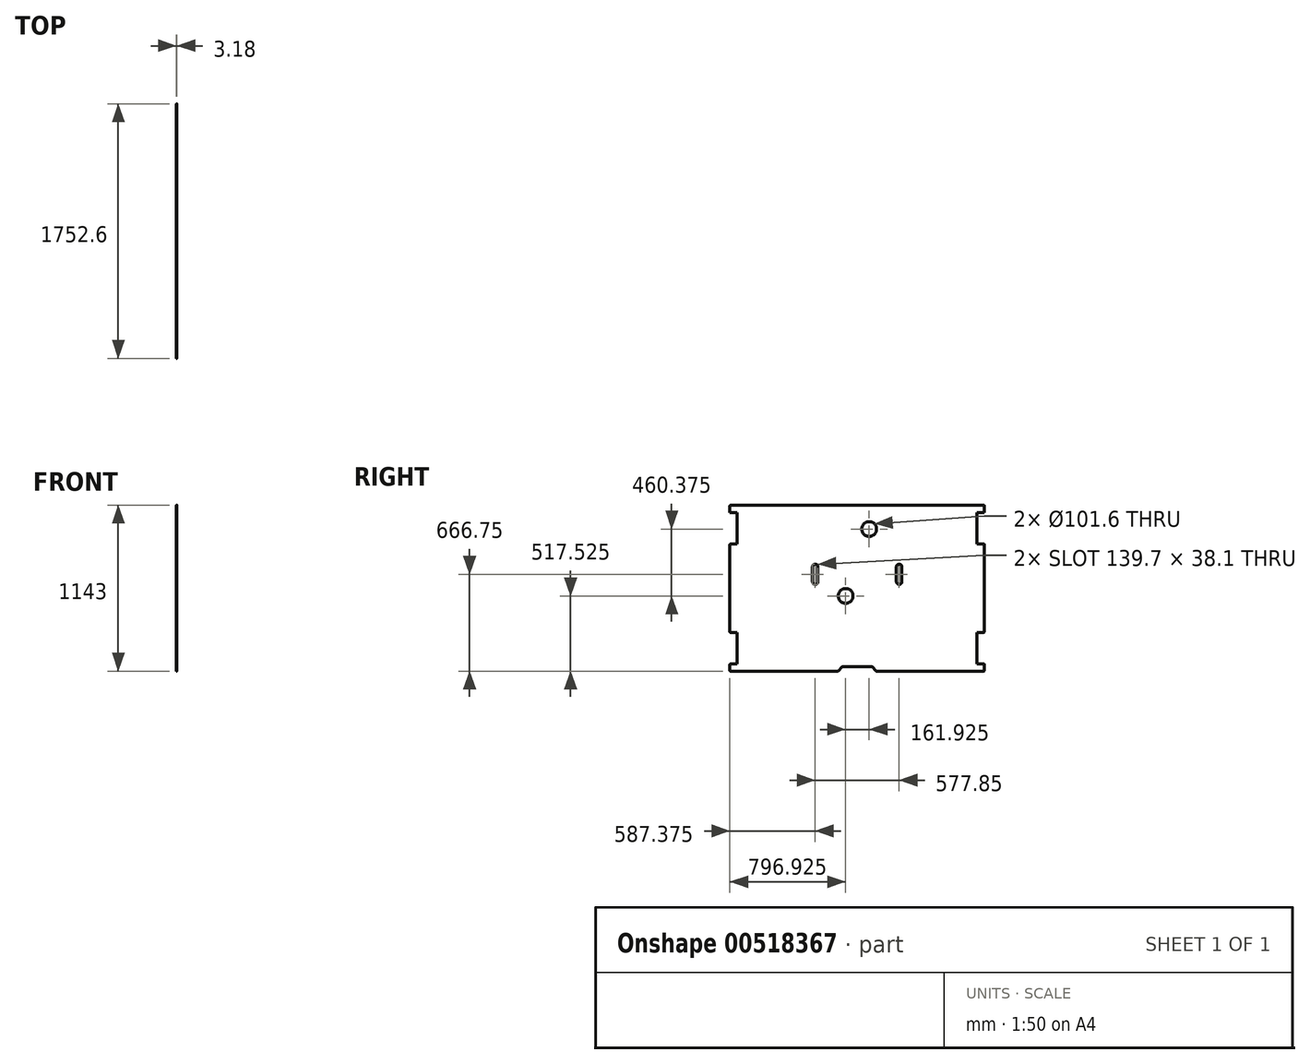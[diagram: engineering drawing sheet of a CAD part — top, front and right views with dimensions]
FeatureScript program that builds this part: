
annotation { "Feature Type Name" : "Feature", "Feature Type Description" : "" }
export const myFeature = defineFeature(function(context is Context, id is Id, definition is map)
    precondition{}
    {
        {
            var Q0;
            Q0=qCreatedBy(makeId("Right.planeOp"),FACE);
            var sketch = newSketch(context, id + "F0", { "sketchPlane" : qUnion([Q0])});
            skLineSegment(sketch, "E0.bottom", {"start": v(-876.3, 571.5) * mm, "end": v(876.3, 571.5) * mm});
            skLineSegment(sketch, "E0.top", {"start": v(-876.3, -571.5) * mm, "end": v(876.3, -571.5) * mm});
            skLineSegment(sketch, "E0.left", {"start": v(-876.3, 571.5) * mm, "end": v(-876.3, -571.5) * mm});
            skLineSegment(sketch, "E0.right", {"start": v(876.3, 571.5) * mm, "end": v(876.3, -571.5) * mm});
            skSolve(sketch);
        }
        {
            var Q0;
            Q0=makeQuery(id+"F0.imprint","IMPRINT",FACE,{"disambiguationData":[TD([[makeQuery(id+"F0.imprint","IMPRINT",EDGE,{"derivedFrom":sQuery(id+"F0.wireOp",EDGE,"E0.bottom")}),-1.0]])]});
            extrude(context, id + "F1", {"entities" : qUnion([Q0]), "endBound" : BoundingType.SYMMETRIC, "depth" : 3.17 * mm, "offsetDistance" : 25.4 * mm});
        }
        {
            var Q0;
            Q0=makeQuery(id+"F1.opExtrude","CAP_FACE",FACE,{"disambiguationData":[OSD([sQuery(id+"F0.wireOp",EDGE,"E0.bottom"),sQuery(id+"F0.wireOp",EDGE,"E0.top"),sQuery(id+"F0.wireOp",EDGE,"E0.left"),sQuery(id+"F0.wireOp",EDGE,"E0.right")])],"isStart":false});
            var sketch = newSketch(context, id + "F2", { "sketchPlane" : qUnion([Q0])});
            skLineSegment(sketch, "E1.bottom", {"start": v(-876.3, 520.7) * mm, "end": v(-825.5, 520.7) * mm});
            skLineSegment(sketch, "E1.top", {"start": v(-876.3, 304.8) * mm, "end": v(-825.5, 304.8) * mm});
            skLineSegment(sketch, "E1.left", {"start": v(-876.3, 520.7) * mm, "end": v(-876.3, 304.8) * mm});
            skLineSegment(sketch, "E1.right", {"start": v(-825.5, 520.7) * mm, "end": v(-825.5, 304.8) * mm});
            skLineSegment(sketch, "E2.MirrorCS", {"start": v(876.3, 304.8) * mm, "end": v(825.5, 304.8) * mm});
            skLineSegment(sketch, "E3.MirrorCS", {"start": v(876.3, 520.7) * mm, "end": v(825.5, 520.7) * mm});
            skLineSegment(sketch, "E4.MirrorCS", {"start": v(876.3, 520.7) * mm, "end": v(876.3, 304.8) * mm});
            skLineSegment(sketch, "E5.MirrorCS", {"start": v(825.5, 520.7) * mm, "end": v(825.5, 304.8) * mm});
            skLineSegment(sketch, "E6.MirrorCS", {"start": v(-876.3, -520.7) * mm, "end": v(-825.5, -520.7) * mm});
            skLineSegment(sketch, "E7.MirrorCS", {"start": v(-876.3, -304.8) * mm, "end": v(-825.5, -304.8) * mm});
            skLineSegment(sketch, "E8.MirrorCS", {"start": v(876.3, -304.8) * mm, "end": v(825.5, -304.8) * mm});
            skLineSegment(sketch, "E9.MirrorCS", {"start": v(876.3, -520.7) * mm, "end": v(825.5, -520.7) * mm});
            skLineSegment(sketch, "E10.MirrorCS", {"start": v(-876.3, -520.7) * mm, "end": v(-876.3, -304.8) * mm});
            skLineSegment(sketch, "E11.MirrorCS", {"start": v(-825.5, -520.7) * mm, "end": v(-825.5, -304.8) * mm});
            skLineSegment(sketch, "E12.MirrorCS", {"start": v(876.3, -520.7) * mm, "end": v(876.3, -304.8) * mm});
            skLineSegment(sketch, "E13.MirrorCS", {"start": v(825.5, -520.7) * mm, "end": v(825.5, -304.8) * mm});
            skSolve(sketch);
        }
        {
            var Q0;
            Q0 = qSketchRegion(id + "F2", true);
            extrude(context, id + "F3", {"entities" : qUnion([Q0]), "operationType" : NewBodyOperationType.REMOVE, "endBound" : BoundingType.THROUGH_ALL, "oppositeDirection" : true, "depth" : 25.4 * mm, "offsetDistance" : 25.4 * mm});
        }
        {
            var Q0;
            Q0=makeQuery(id+"F1.opExtrude","CAP_FACE",FACE,{"disambiguationData":[OSD([sQuery(id+"F0.wireOp",EDGE,"E0.bottom"),sQuery(id+"F0.wireOp",EDGE,"E0.top"),sQuery(id+"F0.wireOp",EDGE,"E0.left"),sQuery(id+"F0.wireOp",EDGE,"E0.right")])],"isStart":false});
            var sketch = newSketch(context, id + "F4", { "sketchPlane" : qUnion([Q0])});
            skArc(sketch, "E14", {"start": v(-269.88, 146.05) * mm, "mid": v(-288.93, 165.1) * mm, "end": v(-307.98, 146.05) * mm});
            skArc(sketch, "E15", {"start": v(-307.97, 44.45) * mm, "mid": v(-288.92, 25.4) * mm, "end": v(-269.88, 44.45) * mm});
            skLineSegment(sketch, "E16", {"start": v(-307.98, 146.05) * mm, "end": v(-307.98, 44.45) * mm});
            skLineSegment(sketch, "E17", {"start": v(-269.88, 146.05) * mm, "end": v(-269.88, 44.45) * mm});
            skLineSegment(sketch, "E18.MirrorCS", {"start": v(269.88, 146.05) * mm, "end": v(269.88, 44.45) * mm});
            skLineSegment(sketch, "E19.MirrorCS", {"start": v(307.98, 146.05) * mm, "end": v(307.98, 44.45) * mm});
            skArc(sketch, "E20.MirrorCS", {"start": v(269.88, 146.05) * mm, "mid": v(288.93, 165.1) * mm, "end": v(307.98, 146.05) * mm});
            skArc(sketch, "E21.MirrorCS", {"start": v(307.97, 44.45) * mm, "mid": v(288.92, 25.4) * mm, "end": v(269.88, 44.45) * mm});
            skSolve(sketch);
        }
        {
            var Q0;
            Q0 = qSketchRegion(id + "F4", true);
            extrude(context, id + "F5", {"entities" : qUnion([Q0]), "operationType" : NewBodyOperationType.REMOVE, "endBound" : BoundingType.THROUGH_ALL, "oppositeDirection" : true, "depth" : 25.4 * mm, "offsetDistance" : 25.4 * mm});
        }
        {
            var Q0;
            Q0=makeQuery(id+"F1.opExtrude","CAP_FACE",FACE,{"disambiguationData":[OSD([sQuery(id+"F0.wireOp",EDGE,"E0.bottom"),sQuery(id+"F0.wireOp",EDGE,"E0.top"),sQuery(id+"F0.wireOp",EDGE,"E0.left"),sQuery(id+"F0.wireOp",EDGE,"E0.right")])],"isStart":false});
            var sketch = newSketch(context, id + "F6", { "sketchPlane" : qUnion([Q0])});
            skCircle(sketch, "E22", {"center": v(82.55, 406.4) * mm, "radius": 50.8 * mm});
            skCircle(sketch, "E23", {"center": v(-79.37, -53.98) * mm, "radius": 50.8 * mm});
            skSolve(sketch);
        }
        {
            var Q0;
            Q0 = qSketchRegion(id + "F6", true);
            extrude(context, id + "F7", {"entities" : qUnion([Q0]), "operationType" : NewBodyOperationType.REMOVE, "endBound" : BoundingType.THROUGH_ALL, "oppositeDirection" : true, "depth" : 25.4 * mm, "offsetDistance" : 25.4 * mm});
        }
        {
            var Q0;
            Q0=makeQuery(id+"F1.opExtrude","CAP_FACE",FACE,{"disambiguationData":[OSD([sQuery(id+"F0.wireOp",EDGE,"E0.bottom"),sQuery(id+"F0.wireOp",EDGE,"E0.top"),sQuery(id+"F0.wireOp",EDGE,"E0.left"),sQuery(id+"F0.wireOp",EDGE,"E0.right")])],"isStart":false});
            var sketch = newSketch(context, id + "F8", { "sketchPlane" : qUnion([Q0])});
            skLineSegment(sketch, "E24", {"start": v(-130.17, -571.5) * mm, "end": v(-101.6, -539.75) * mm});
            skLineSegment(sketch, "E25", {"start": v(-101.6, -539.75) * mm, "end": v(101.6, -539.75) * mm});
            skLineSegment(sketch, "E26", {"start": v(101.6, -539.75) * mm, "end": v(130.18, -571.5) * mm});
            skLineSegment(sketch, "E27", {"start": v(130.18, -571.5) * mm, "end": v(-130.18, -571.5) * mm});
            skSolve(sketch);
        }
        {
            var Q0;
            Q0 = qSketchRegion(id + "F8", true);
            extrude(context, id + "F9", {"entities" : qUnion([Q0]), "operationType" : NewBodyOperationType.REMOVE, "endBound" : BoundingType.THROUGH_ALL, "oppositeDirection" : true, "depth" : 25.4 * mm, "offsetDistance" : 25.4 * mm});
        }
        {
            var Q0;
            Q0=makeQuery(id+"F1.opExtrude","SWEPT_EDGE",EDGE,{"disambiguationData":[OSD([sQuery(id+"F0.wireOp",EDGE,"E0.top"),sQuery(id+"F0.wireOp",EDGE,"E0.left")])]});
            var Q1;
            Q1=makeQuery(id+"F3.boolean.opBoolean","COPY",EDGE,{"derivedFrom":makeQuery(id+"F3.opExtrude","SWEPT_EDGE",EDGE,{"disambiguationData":[OSD([sQuery(id+"F0.wireOp",EDGE,"E0.left"),sQuery(id+"F2.wireOp",EDGE,"E6.MirrorCS"),sQuery(id+"F2.wireOp",EDGE,"E10.MirrorCS")])]})});
            var Q2;
            Q2=makeQuery(id+"F3.boolean.opBoolean","COPY",EDGE,{"derivedFrom":makeQuery(id+"F3.opExtrude","SWEPT_EDGE",EDGE,{"disambiguationData":[OSD([sQuery(id+"F0.wireOp",EDGE,"E0.left"),sQuery(id+"F2.wireOp",EDGE,"E7.MirrorCS"),sQuery(id+"F2.wireOp",EDGE,"E10.MirrorCS")])]})});
            var Q3;
            Q3=makeQuery(id+"F3.boolean.opBoolean","COPY",EDGE,{"derivedFrom":makeQuery(id+"F3.opExtrude","SWEPT_EDGE",EDGE,{"disambiguationData":[OSD([sQuery(id+"F0.wireOp",EDGE,"E0.left"),sQuery(id+"F2.wireOp",EDGE,"E1.top"),sQuery(id+"F2.wireOp",EDGE,"E1.left")])]})});
            var Q4;
            Q4=makeQuery(id+"F3.boolean.opBoolean","COPY",EDGE,{"derivedFrom":makeQuery(id+"F3.opExtrude","SWEPT_EDGE",EDGE,{"disambiguationData":[OSD([sQuery(id+"F0.wireOp",EDGE,"E0.left"),sQuery(id+"F2.wireOp",EDGE,"E1.bottom"),sQuery(id+"F2.wireOp",EDGE,"E1.left")])]})});
            var Q5;
            Q5=makeQuery(id+"F1.opExtrude","SWEPT_EDGE",EDGE,{"disambiguationData":[OSD([sQuery(id+"F0.wireOp",EDGE,"E0.bottom"),sQuery(id+"F0.wireOp",EDGE,"E0.left")])]});
            var Q6;
            Q6=makeQuery(id+"F1.opExtrude","SWEPT_EDGE",EDGE,{"disambiguationData":[OSD([sQuery(id+"F0.wireOp",EDGE,"E0.bottom"),sQuery(id+"F0.wireOp",EDGE,"E0.right")])]});
            var Q7;
            Q7=makeQuery(id+"F3.boolean.opBoolean","COPY",EDGE,{"derivedFrom":makeQuery(id+"F3.opExtrude","SWEPT_EDGE",EDGE,{"disambiguationData":[OSD([sQuery(id+"F0.wireOp",EDGE,"E0.right"),sQuery(id+"F2.wireOp",EDGE,"E3.MirrorCS"),sQuery(id+"F2.wireOp",EDGE,"E4.MirrorCS")])]})});
            var Q8;
            Q8=makeQuery(id+"F3.boolean.opBoolean","COPY",EDGE,{"derivedFrom":makeQuery(id+"F3.opExtrude","SWEPT_EDGE",EDGE,{"disambiguationData":[OSD([sQuery(id+"F0.wireOp",EDGE,"E0.right"),sQuery(id+"F2.wireOp",EDGE,"E2.MirrorCS"),sQuery(id+"F2.wireOp",EDGE,"E4.MirrorCS")])]})});
            var Q9;
            Q9=makeQuery(id+"F3.boolean.opBoolean","COPY",EDGE,{"derivedFrom":makeQuery(id+"F3.opExtrude","SWEPT_EDGE",EDGE,{"disambiguationData":[OSD([sQuery(id+"F0.wireOp",EDGE,"E0.right"),sQuery(id+"F2.wireOp",EDGE,"E8.MirrorCS"),sQuery(id+"F2.wireOp",EDGE,"E12.MirrorCS")])]})});
            var Q10;
            Q10=makeQuery(id+"F3.boolean.opBoolean","COPY",EDGE,{"derivedFrom":makeQuery(id+"F3.opExtrude","SWEPT_EDGE",EDGE,{"disambiguationData":[OSD([sQuery(id+"F0.wireOp",EDGE,"E0.right"),sQuery(id+"F2.wireOp",EDGE,"E9.MirrorCS"),sQuery(id+"F2.wireOp",EDGE,"E12.MirrorCS")])]})});
            var Q11;
            Q11=makeQuery(id+"F1.opExtrude","SWEPT_EDGE",EDGE,{"disambiguationData":[OSD([sQuery(id+"F0.wireOp",EDGE,"E0.top"),sQuery(id+"F0.wireOp",EDGE,"E0.right")])]});
            var Q12;
            Q12=makeQuery(id+"F9.boolean.opBoolean","COPY",EDGE,{"derivedFrom":makeQuery(id+"F9.opExtrude","SWEPT_EDGE",EDGE,{"disambiguationData":[OSD([sQuery(id+"F0.wireOp",EDGE,"E0.top"),sQuery(id+"F8.wireOp",EDGE,"E26"),sQuery(id+"F8.wireOp",EDGE,"E27")])]})});
            var Q13;
            Q13=makeQuery(id+"F9.boolean.opBoolean","COPY",EDGE,{"derivedFrom":makeQuery(id+"F9.opExtrude","SWEPT_EDGE",EDGE,{"disambiguationData":[OSD([sQuery(id+"F0.wireOp",EDGE,"E0.top"),sQuery(id+"F8.wireOp",EDGE,"E24"),sQuery(id+"F8.wireOp",EDGE,"E27")])]})});
            var Q14;
            Q14=makeQuery(id+"F9.boolean.opBoolean","COPY",EDGE,{"derivedFrom":makeQuery(id+"F9.opExtrude","SWEPT_EDGE",EDGE,{"disambiguationData":[OSD([sQuery(id+"F8.wireOp",EDGE,"E24"),sQuery(id+"F8.wireOp",EDGE,"E25")])]})});
            var Q15;
            Q15=makeQuery(id+"F9.boolean.opBoolean","COPY",EDGE,{"derivedFrom":makeQuery(id+"F9.opExtrude","SWEPT_EDGE",EDGE,{"disambiguationData":[OSD([sQuery(id+"F8.wireOp",EDGE,"E25"),sQuery(id+"F8.wireOp",EDGE,"E26")])]})});
            fillet(context, id + "F10", {"entities" : qUnion([Q0, Q1, Q2, Q3, Q4, Q5, Q6, Q7, Q8, Q9, Q10, Q11, Q12, Q13, Q14, Q15]), "radius" : 5.08 * mm, "tangentPropagation" : true, "allowEdgeOverflow" : false});
        }
    });
